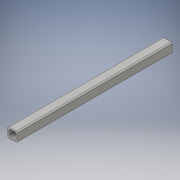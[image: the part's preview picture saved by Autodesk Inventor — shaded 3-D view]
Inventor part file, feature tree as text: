
AUTODESK INVENTOR PART (.ipt)
format: ipt  version: 2016 (Build 200138000, 138)  size: 112,640 bytes
history: native  units: in
note: dims shown in document units (in); Inventor stores cm internally (conversion verified against a paired STEP export)
features: extrude x1, sketch x1
ambient origin geometry x8: Origin, YZ Plane, XZ Plane, XY Plane, X Axis, Y Axis, Z Axis, Center Point
bodies: Solid1 (feature_tree)
feature tree (2):
  extrude  "Extrusion1"  Depth=1.0in
  sketch  "Sketch1"  dims[d0=1.0in d1=1.0in d2=0.125in d3=0.125in d4=16.0in d5=0.0in]
